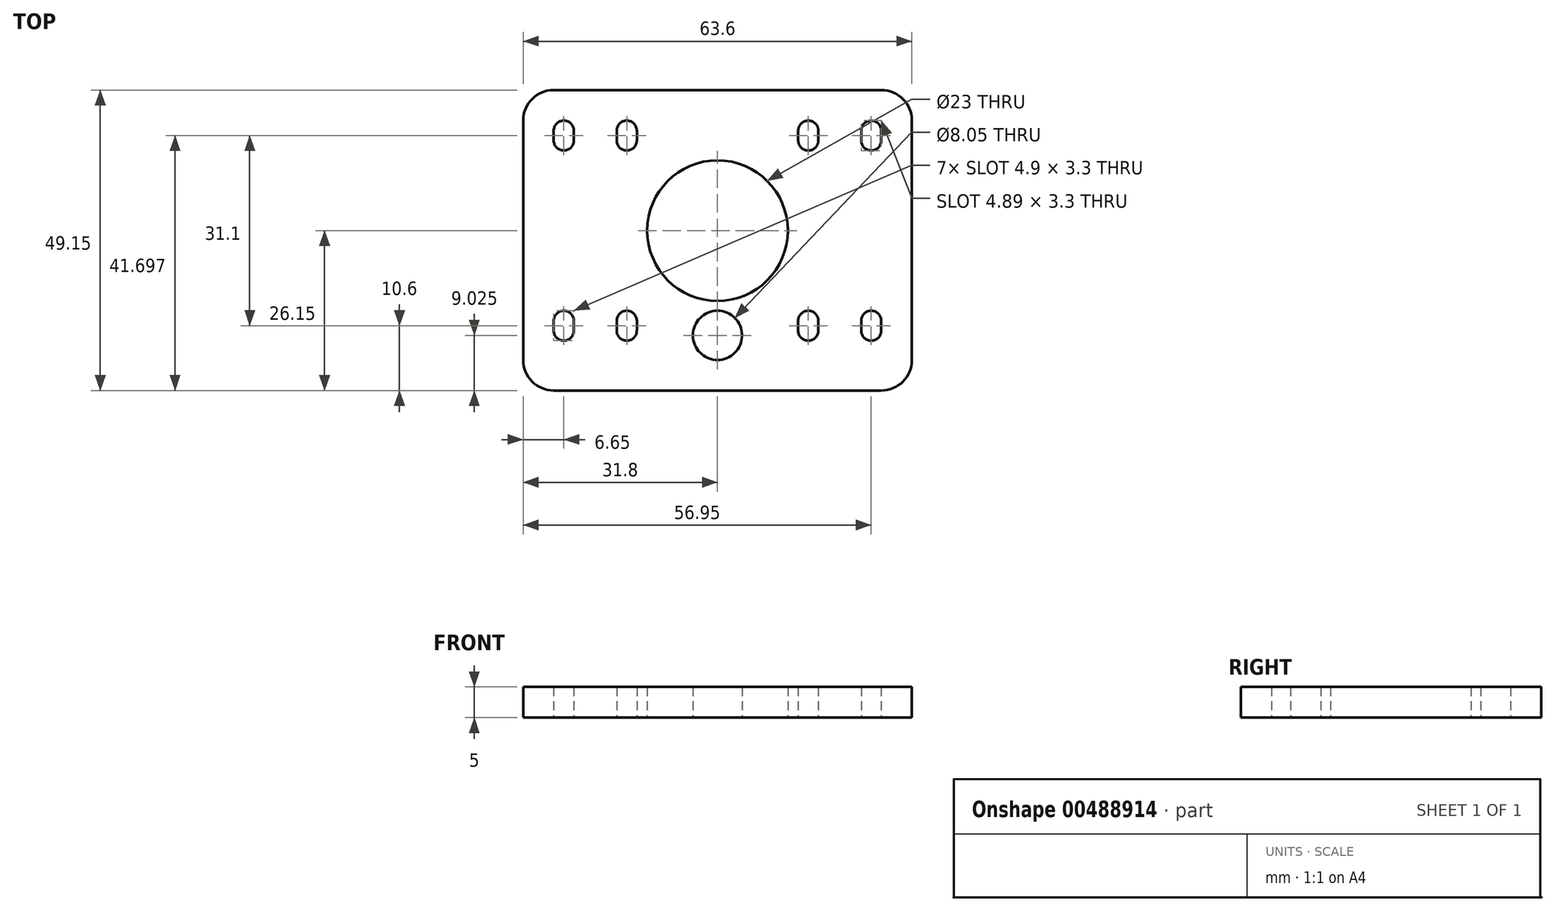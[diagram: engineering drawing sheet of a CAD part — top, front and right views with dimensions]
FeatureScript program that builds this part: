
annotation { "Feature Type Name" : "Feature", "Feature Type Description" : "" }
export const myFeature = defineFeature(function(context is Context, id is Id, definition is map)
    precondition{}
    {
        {
            var Q0;
            Q0=qCreatedBy(makeId("Top.planeOp"),FACE);
            var sketch = newSketch(context, id + "F0", { "sketchPlane" : qUnion([Q0])});
            skLineSegment(sketch, "E0.bottom", {"start": v(-21.5, 23) * mm, "end": v(21.5, 23) * mm});
            skLineSegment(sketch, "E0.top", {"start": v(-21.5, -23) * mm, "end": v(21.5, -23) * mm});
            skLineSegment(sketch, "E0.left", {"start": v(-21.5, 23) * mm, "end": v(-21.5, -23) * mm});
            skLineSegment(sketch, "E0.right", {"start": v(21.5, 23) * mm, "end": v(21.5, -23) * mm});
            skPoint(sketch, "E0.middle", {"position": v(0, 0) * mm});
            skCircle(sketch, "E1", {"center": v(0, 0) * mm, "radius": 11.5 * mm});
            skCircle(sketch, "E2", {"center": v(-14.85, 16.35) * mm, "radius": 1.65 * mm});
            skCircle(sketch, "E3", {"center": v(14.85, 16.35) * mm, "radius": 1.65 * mm});
            skCircle(sketch, "E4", {"center": v(14.85, -16.35) * mm, "radius": 1.65 * mm});
            skCircle(sketch, "E5", {"center": v(-14.85, -16.35) * mm, "radius": 1.65 * mm});
            skCircle(sketch, "E6", {"center": v(-14.85, -14.75) * mm, "radius": 1.65 * mm});
            skCircle(sketch, "E7", {"center": v(-14.85, 14.75) * mm, "radius": 1.65 * mm});
            skCircle(sketch, "E8", {"center": v(14.85, 14.75) * mm, "radius": 1.65 * mm});
            skCircle(sketch, "E9", {"center": v(14.85, -14.75) * mm, "radius": 1.65 * mm});
            skLineSegment(sketch, "E10", {"start": v(13.2, -14.75) * mm, "end": v(16.5, -14.75) * mm});
            skLineSegment(sketch, "E11", {"start": v(16.5, -14.75) * mm, "end": v(16.5, -16.35) * mm});
            skLineSegment(sketch, "E12", {"start": v(16.5, -16.35) * mm, "end": v(13.2, -16.35) * mm});
            skLineSegment(sketch, "E13", {"start": v(13.2, -16.35) * mm, "end": v(13.2, -14.75) * mm});
            skLineSegment(sketch, "E14", {"start": v(-16.5, -14.75) * mm, "end": v(-13.2, -14.74) * mm});
            skLineSegment(sketch, "E15", {"start": v(-16.5, -14.75) * mm, "end": v(-16.5, -16.35) * mm});
            skLineSegment(sketch, "E16", {"start": v(-16.5, -16.35) * mm, "end": v(-13.2, -16.34) * mm});
            skLineSegment(sketch, "E17", {"start": v(-13.2, -16.34) * mm, "end": v(-13.2, -14.74) * mm});
            skLineSegment(sketch, "E18", {"start": v(-16.5, 16.35) * mm, "end": v(-13.2, 16.35) * mm});
            skLineSegment(sketch, "E19", {"start": v(-13.2, 16.35) * mm, "end": v(-13.2, 14.75) * mm});
            skLineSegment(sketch, "E20", {"start": v(-13.2, 14.75) * mm, "end": v(-16.5, 14.75) * mm});
            skLineSegment(sketch, "E21", {"start": v(-16.5, 14.75) * mm, "end": v(-16.5, 16.35) * mm});
            skLineSegment(sketch, "E22", {"start": v(13.2, 16.35) * mm, "end": v(16.5, 16.34) * mm});
            skLineSegment(sketch, "E23", {"start": v(16.5, 16.34) * mm, "end": v(16.5, 14.75) * mm});
            skLineSegment(sketch, "E24", {"start": v(16.5, 14.75) * mm, "end": v(13.2, 14.75) * mm});
            skLineSegment(sketch, "E25", {"start": v(13.2, 14.75) * mm, "end": v(13.2, 16.35) * mm});
            skCircle(sketch, "E26", {"center": v(0, -17.12) * mm, "radius": 4.03 * mm});
            skLineSegment(sketch, "E27", {"start": v(-21.5, -26.15) * mm, "end": v(21.5, -26.15) * mm});
            skLineSegment(sketch, "E28", {"start": v(-21.5, -26.15) * mm, "end": v(-21.5, -23) * mm});
            skLineSegment(sketch, "E29", {"start": v(21.5, -26.15) * mm, "end": v(21.5, -23) * mm});
            skCircle(sketch, "E30", {"center": v(-25.15, -16.35) * mm, "radius": 1.65 * mm});
            skCircle(sketch, "E31", {"center": v(-25.15, -14.75) * mm, "radius": 1.65 * mm});
            skLineSegment(sketch, "E32", {"start": v(-26.8, -14.75) * mm, "end": v(-23.5, -14.75) * mm});
            skLineSegment(sketch, "E33", {"start": v(-23.5, -14.75) * mm, "end": v(-23.5, -16.35) * mm});
            skLineSegment(sketch, "E34", {"start": v(-23.5, -16.35) * mm, "end": v(-26.8, -16.35) * mm});
            skLineSegment(sketch, "E35", {"start": v(-26.8, -16.35) * mm, "end": v(-26.8, -14.75) * mm});
            skCircle(sketch, "E36", {"center": v(-25.15, 14.75) * mm, "radius": 1.65 * mm});
            skCircle(sketch, "E37", {"center": v(-25.15, 16.35) * mm, "radius": 1.65 * mm});
            skLineSegment(sketch, "E38", {"start": v(-26.8, 16.35) * mm, "end": v(-23.5, 16.35) * mm});
            skLineSegment(sketch, "E39", {"start": v(-23.5, 16.35) * mm, "end": v(-23.5, 14.75) * mm});
            skLineSegment(sketch, "E40", {"start": v(-23.5, 14.75) * mm, "end": v(-26.8, 14.75) * mm});
            skLineSegment(sketch, "E41", {"start": v(-26.8, 14.75) * mm, "end": v(-26.8, 16.35) * mm});
            skCircle(sketch, "E42", {"center": v(25.15, 14.75) * mm, "radius": 1.65 * mm});
            skCircle(sketch, "E43", {"center": v(25.15, 16.34) * mm, "radius": 1.65 * mm});
            skLineSegment(sketch, "E44", {"start": v(23.5, 16.34) * mm, "end": v(26.8, 16.34) * mm});
            skLineSegment(sketch, "E45", {"start": v(26.8, 16.34) * mm, "end": v(26.8, 14.75) * mm});
            skLineSegment(sketch, "E46", {"start": v(26.8, 14.75) * mm, "end": v(23.5, 14.75) * mm});
            skLineSegment(sketch, "E47", {"start": v(23.5, 14.75) * mm, "end": v(23.5, 16.34) * mm});
            skCircle(sketch, "E48", {"center": v(25.15, -16.35) * mm, "radius": 1.65 * mm});
            skCircle(sketch, "E49", {"center": v(25.15, -14.75) * mm, "radius": 1.65 * mm});
            skLineSegment(sketch, "E50", {"start": v(23.5, -14.75) * mm, "end": v(26.8, -14.75) * mm});
            skLineSegment(sketch, "E51", {"start": v(26.8, -14.75) * mm, "end": v(26.8, -16.35) * mm});
            skLineSegment(sketch, "E52", {"start": v(26.8, -16.35) * mm, "end": v(23.5, -16.35) * mm});
            skLineSegment(sketch, "E53", {"start": v(23.5, -16.35) * mm, "end": v(23.5, -14.75) * mm});
            skLineSegment(sketch, "E54", {"start": v(-31.8, 23) * mm, "end": v(-31.8, -26.15) * mm});
            skLineSegment(sketch, "E55", {"start": v(31.8, 23) * mm, "end": v(31.8, -26.15) * mm});
            skLineSegment(sketch, "E56", {"start": v(21.5, 23) * mm, "end": v(31.8, 23) * mm});
            skLineSegment(sketch, "E57", {"start": v(-21.5, 23) * mm, "end": v(-31.8, 23) * mm});
            skLineSegment(sketch, "E58", {"start": v(21.5, -26.15) * mm, "end": v(31.8, -26.15) * mm});
            skLineSegment(sketch, "E59", {"start": v(-21.5, -26.15) * mm, "end": v(-31.8, -26.15) * mm});
            skSolve(sketch);
        }
        {
            var Q0;
            Q0=makeQuery(id+"F0.imprint","IMPRINT",FACE,{"disambiguationData":[TD([[makeQuery(id+"F0.imprint","IMPRINT",EDGE,{"derivedFrom":sQuery(id+"F0.wireOp",EDGE,"E0.left")}),-1.0]])]});
            var Q1;
            Q1=makeQuery(id+"F0.imprint","IMPRINT",FACE,{"disambiguationData":[TD([[makeQuery(id+"F0.imprint","IMPRINT",EDGE,{"derivedFrom":sQuery(id+"F0.wireOp",EDGE,"E0.bottom")}),-1.0]])]});
            var Q2;
            Q2=makeQuery(id+"F0.imprint","IMPRINT",FACE,{"disambiguationData":[TD([[makeQuery(id+"F0.imprint","IMPRINT",EDGE,{"derivedFrom":sQuery(id+"F0.wireOp",EDGE,"E0.top")}),-1.0]])]});
            var Q3;
            Q3=makeQuery(id+"F0.imprint","IMPRINT",FACE,{"disambiguationData":[TD([[makeQuery(id+"F0.imprint","IMPRINT",EDGE,{"derivedFrom":sQuery(id+"F0.wireOp",EDGE,"E0.right")}),1.0]])]});
            extrude(context, id + "F1", {"entities" : qUnion([Q0, Q1, Q2, Q3]), "depth" : 5 * mm});
        }
        {
            var Q0;
            Q0=makeQuery(id+"F1.opExtrude","SWEPT_EDGE",EDGE,{"disambiguationData":[OSD([sQuery(id+"F0.wireOp",EDGE,"E54"),sQuery(id+"F0.wireOp",EDGE,"E57")])]});
            var Q1;
            Q1=makeQuery(id+"F1.opExtrude","SWEPT_EDGE",EDGE,{"disambiguationData":[OSD([sQuery(id+"F0.wireOp",EDGE,"E54"),sQuery(id+"F0.wireOp",EDGE,"E59")])]});
            var Q2;
            Q2=makeQuery(id+"F1.opExtrude","SWEPT_EDGE",EDGE,{"disambiguationData":[OSD([sQuery(id+"F0.wireOp",EDGE,"E55"),sQuery(id+"F0.wireOp",EDGE,"E58")])]});
            var Q3;
            Q3=makeQuery(id+"F1.opExtrude","SWEPT_EDGE",EDGE,{"disambiguationData":[OSD([sQuery(id+"F0.wireOp",EDGE,"E55"),sQuery(id+"F0.wireOp",EDGE,"E56")])]});
            fillet(context, id + "F2", {"entities" : qUnion([Q0, Q1, Q2, Q3]), "radius" : 5 * mm, "tangentPropagation" : true, "allowEdgeOverflow" : false});
        }
    });
